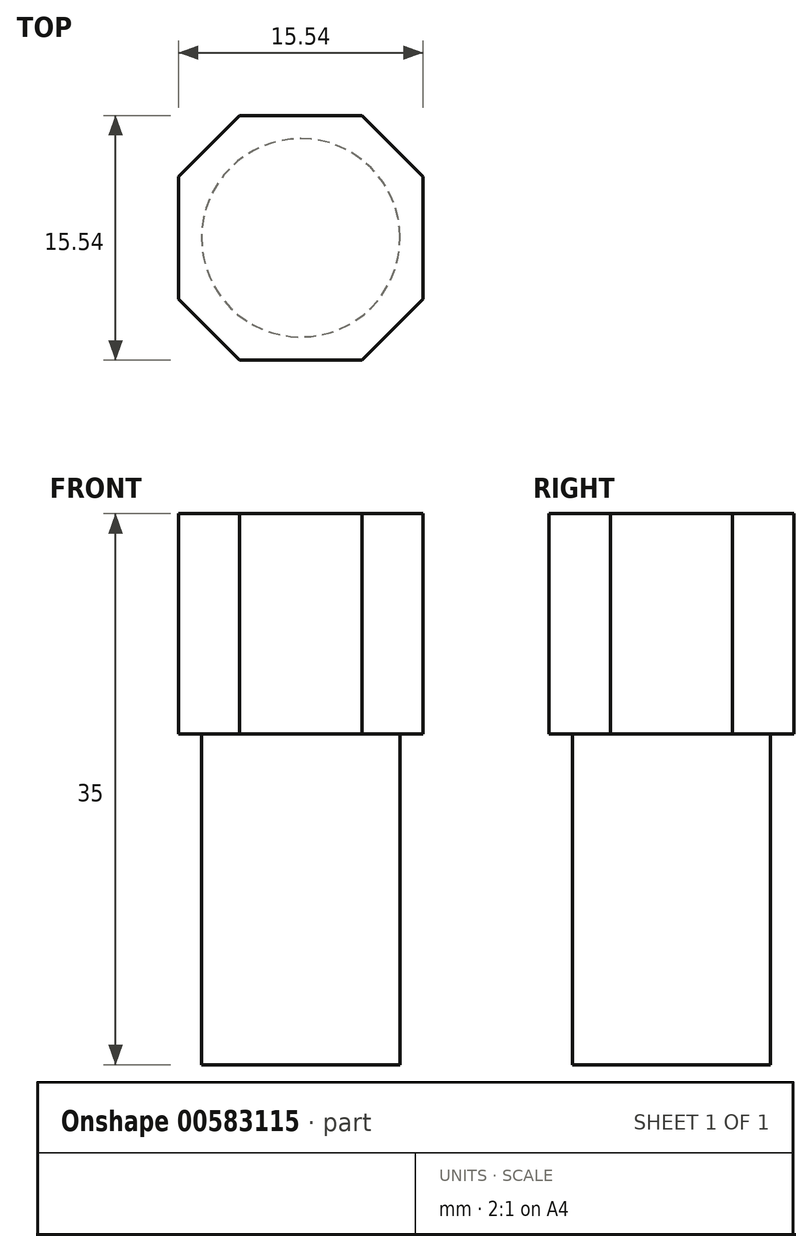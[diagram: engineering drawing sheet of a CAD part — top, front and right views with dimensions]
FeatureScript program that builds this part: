
annotation { "Feature Type Name" : "Feature", "Feature Type Description" : "" }
export const myFeature = defineFeature(function(context is Context, id is Id, definition is map)
    precondition{}
    {
        {
            var Q0;
            Q0=qCreatedBy(makeId("Top.planeOp"),FACE);
            var sketch = newSketch(context, id + "F0", { "sketchPlane" : qUnion([Q0])});
            skLineSegment(sketch, "E0", {"start": v(0, 0) * mm, "end": v(0, -7.77) * mm});
            skLineSegment(sketch, "E1", {"start": v(0, -7.77) * mm, "end": v(3.89, -7.77) * mm});
            skLineSegment(sketch, "E2", {"start": v(7.78, -3.89) * mm, "end": v(7.78, 3.89) * mm});
            skLineSegment(sketch, "E3", {"start": v(3.89, 7.78) * mm, "end": v(-3.89, 7.78) * mm});
            skLineSegment(sketch, "E4", {"start": v(-7.78, 3.89) * mm, "end": v(-7.78, -3.89) * mm});
            skLineSegment(sketch, "E5", {"start": v(-3.89, -7.77) * mm, "end": v(0, -7.77) * mm});
            skLineSegment(sketch, "E6", {"start": v(-3.89, -7.77) * mm, "end": v(-7.78, -3.89) * mm});
            skLineSegment(sketch, "E7", {"start": v(3.89, -7.78) * mm, "end": v(7.78, -3.89) * mm});
            skPoint(sketch, "E8.orphan", {"position": v(-7.78, -7.77) * mm});
            skPoint(sketch, "E9.orphan", {"position": v(7.78, -7.77) * mm});
            skLineSegment(sketch, "E10", {"start": v(-3.89, 7.78) * mm, "end": v(-7.78, 3.89) * mm});
            skLineSegment(sketch, "E11", {"start": v(7.78, 3.89) * mm, "end": v(3.89, 7.77) * mm});
            skPoint(sketch, "E12", {"position": v(7.78, 0) * mm});
            skSolve(sketch);
        }
        {
            var Q0;
            Q0=qSketchRegion(id+"F0",true);
            extrude(context, id + "F1", {"entities" : qUnion([Q0]), "depth" : 14 * mm, "offsetDistance" : 25 * mm});
        }
        {
            var Q0;
            Q0=makeQuery(id+"F1.opExtrude","CAP_FACE",FACE,{"disambiguationData":[OSD([sQuery(id+"F0.wireOp",EDGE,"E1"),sQuery(id+"F0.wireOp",EDGE,"E2"),sQuery(id+"F0.wireOp",EDGE,"E3"),sQuery(id+"F0.wireOp",EDGE,"E4"),sQuery(id+"F0.wireOp",EDGE,"E5"),sQuery(id+"F0.wireOp",EDGE,"E6"),sQuery(id+"F0.wireOp",EDGE,"E7"),sQuery(id+"F0.wireOp",EDGE,"E10"),sQuery(id+"F0.wireOp",EDGE,"E11")])],"isStart":true});
            var sketch = newSketch(context, id + "F2", { "sketchPlane" : qUnion([Q0])});
            skCircle(sketch, "E13", {"center": v(0, 0) * mm, "radius": 6.3 * mm});
            skSolve(sketch);
        }
        {
            var Q0;
            Q0=makeQuery(id+"F2.imprint","IMPRINT",FACE,{"disambiguationData":[TD([[makeQuery(id+"F2.imprint","IMPRINT",EDGE,{"derivedFrom":sQuery(id+"F2.wireOp",EDGE,"E13")}),1.0]])]});
            extrude(context, id + "F3", {"entities" : qUnion([Q0]), "operationType" : NewBodyOperationType.ADD, "depth" : 21 * mm, "offsetDistance" : 25 * mm});
        }
    });
